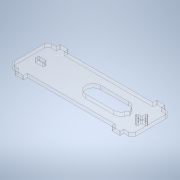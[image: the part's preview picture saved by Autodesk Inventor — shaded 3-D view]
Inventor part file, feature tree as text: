
AUTODESK INVENTOR PART (.ipt)
format: ipt  version: 2021 (Build 250183000, 183)  size: 217,600 bytes
history: native  units: mm
features: extrude x1, sketch x1
ambient origin geometry x8: Origin, YZ Plane, XZ Plane, XY Plane, X Axis, Y Axis, Z Axis, Center Point
bodies: Solid1 (feature_tree)
feature tree (2):
  extrude  "Extrusion1"  Depth=0.5mm
  sketch  "Sketch1"  dims[d2=0.5mm d4=0.5mm d24=2.0mm d25=0.0mm d38=2.0mm d40=0.25mm d41=47.0mm d42=47.0mm d43=56.0mm d44=15.0mm d45=15.75mm d46=8.0mm d47=0.5mm]
